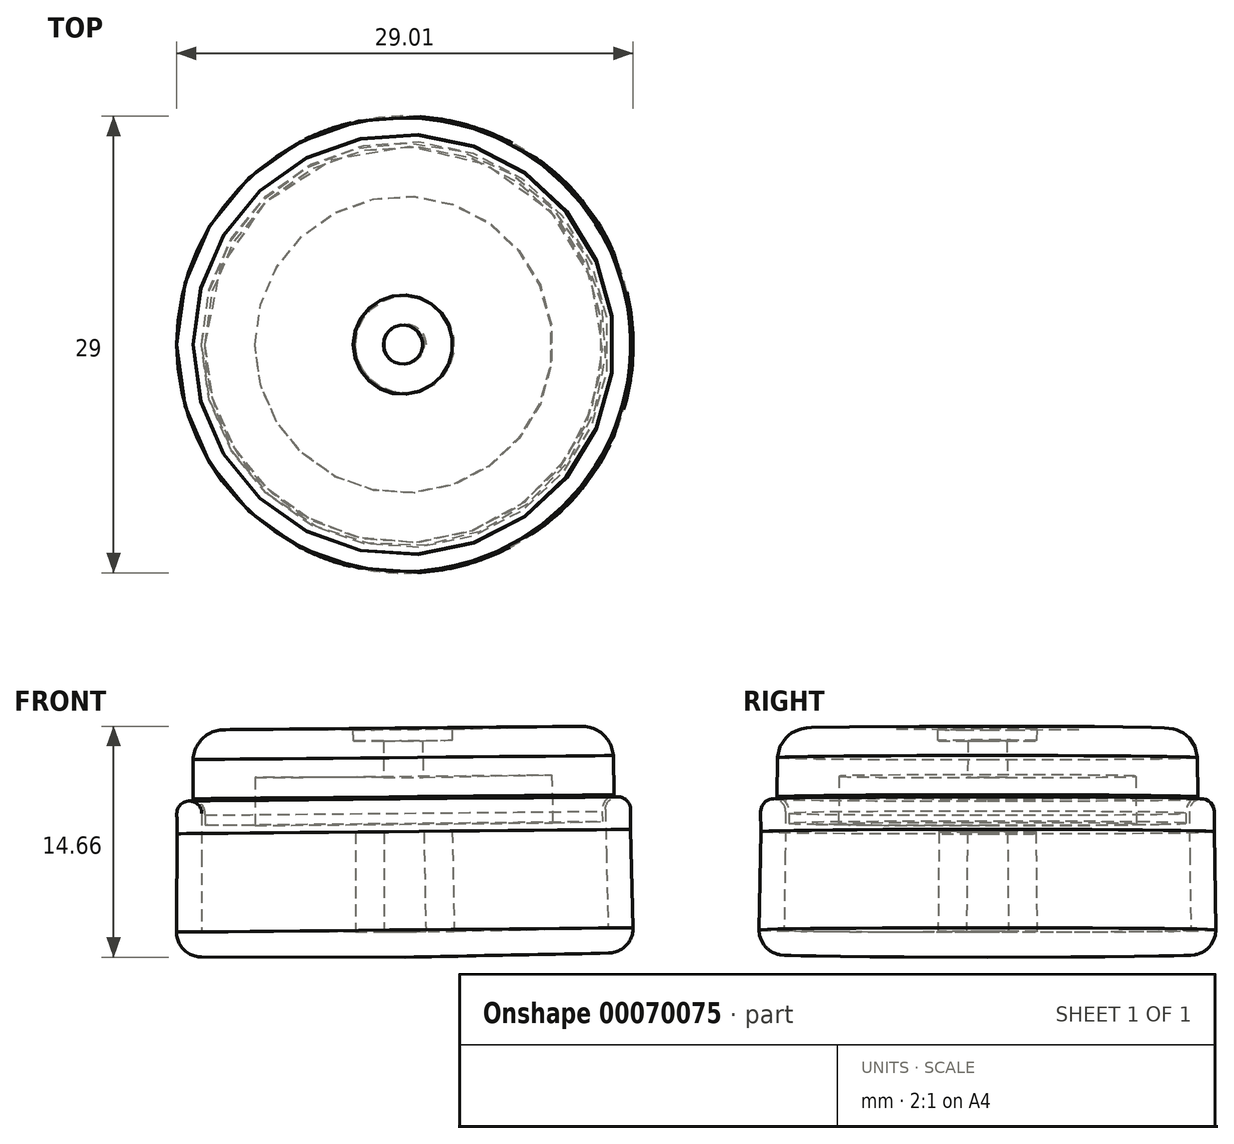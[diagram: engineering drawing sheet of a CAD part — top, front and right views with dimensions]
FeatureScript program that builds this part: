
annotation { "Feature Type Name" : "Feature", "Feature Type Description" : "" }
export const myFeature = defineFeature(function(context is Context, id is Id, definition is map)
    precondition{}
    {
        {
            var Q0;
            Q0=qCreatedBy(makeId("Front.planeOp"),FACE);
            var sketch = newSketch(context, id + "F0", { "sketchPlane" : qUnion([Q0])});
            skLineSegment(sketch, "E0", {"start": v(-3.15, 7.94) * mm, "end": v(-3.15, 1.6) * mm});
            skLineSegment(sketch, "E1", {"start": v(-1.35, 7.95) * mm, "end": v(-1.35, 1.6) * mm});
            skLineSegment(sketch, "E2", {"start": v(-1.35, 7.95) * mm, "end": v(-3.15, 7.94) * mm});
            skLineSegment(sketch, "E3", {"start": v(-12.9, 9.13) * mm, "end": v(-12.9, 6.49) * mm});
            skLineSegment(sketch, "E4", {"start": v(-12.9, 6.49) * mm, "end": v(-12.93, 1.6) * mm});
            skLineSegment(sketch, "E5", {"start": v(-14.5, 9.11) * mm, "end": v(-14.47, 7.84) * mm});
            skLineSegment(sketch, "E6", {"start": v(-14.47, 7.84) * mm, "end": v(-14.52, 1.6) * mm});
            skLineSegment(sketch, "E7", {"start": v(0, 0) * mm, "end": v(-12.93, 0.01) * mm});
            skLineSegment(sketch, "E8", {"start": v(-3.15, 1.6) * mm, "end": v(-12.93, 1.6) * mm});
            skLineSegment(sketch, "E9", {"start": v(-0.02, 1.6) * mm, "end": v(-1.35, 1.6) * mm});
            skLineSegment(sketch, "E10", {"start": v(0, 0) * mm, "end": v(-0.02, 1.6) * mm});
            skArc(sketch, "E11", {"start": v(-12.9, 9.13) * mm, "mid": v(-13.7, 9.92) * mm, "end": v(-14.5, 9.11) * mm});
            skArc(sketch, "E12", {"start": v(-14.52, 1.6) * mm, "mid": v(-14.05, 0.47) * mm, "end": v(-12.93, 0.01) * mm});
            skSolve(sketch);
        }
        {
            var Q0;
            Q0=qCreatedBy(makeId("Front.planeOp"),FACE);
            var sketch = newSketch(context, id + "F1", { "sketchPlane" : qUnion([Q0])});
            skLineSegment(sketch, "E13", {"start": v(-9.54, 8.36) * mm, "end": v(-12.7, 8.39) * mm});
            skLineSegment(sketch, "E14", {"start": v(-12.7, 8.39) * mm, "end": v(-12.7, 9.02) * mm});
            skLineSegment(sketch, "E15", {"start": v(-9.54, 11.4) * mm, "end": v(-9.54, 8.36) * mm});
            skLineSegment(sketch, "E16", {"start": v(-9.54, 11.4) * mm, "end": v(-1.37, 11.4) * mm});
            skLineSegment(sketch, "E17", {"start": v(-13.47, 12.55) * mm, "end": v(-13.47, 10.06) * mm});
            skArc(sketch, "E18", {"start": v(-12.7, 9.02) * mm, "mid": v(-12.9, 9.68) * mm, "end": v(-13.47, 10.06) * mm});
            skArc(sketch, "E19", {"start": v(-11.47, 14.45) * mm, "mid": v(-12.85, 13.9) * mm, "end": v(-13.47, 12.55) * mm});
            skLineSegment(sketch, "E20", {"start": v(-1.37, 11.4) * mm, "end": v(-1.37, 13.73) * mm});
            skLineSegment(sketch, "E21", {"start": v(-11.47, 14.45) * mm, "end": v(-3.3, 14.44) * mm});
            skLineSegment(sketch, "E22", {"start": v(-3.3, 14.44) * mm, "end": v(-3.27, 13.73) * mm});
            skLineSegment(sketch, "E23", {"start": v(-3.27, 13.73) * mm, "end": v(-1.37, 13.73) * mm});
            skSolve(sketch);
        }
        {
            var Q0;
            Q0 = qSketchRegion(id + "F0", true);
            var Q1;
            Q1=sQuery(id+"F0.wireOp",EDGE,"E10");
            revolve(context, id + "F2", {"entities" : qUnion([Q0]), "axis" : qUnion([Q1]), "revolveType" : RevolveType.FULL});
        }
        {
            var Q0;
            Q0 = qSketchRegion(id + "F1", true);
            var Q1;
            Q1=sQuery(id+"F0.wireOp",EDGE,"E10");
            revolve(context, id + "F3", {"entities" : qUnion([Q0]), "axis" : qUnion([Q1]), "revolveType" : RevolveType.FULL});
        }
    });
